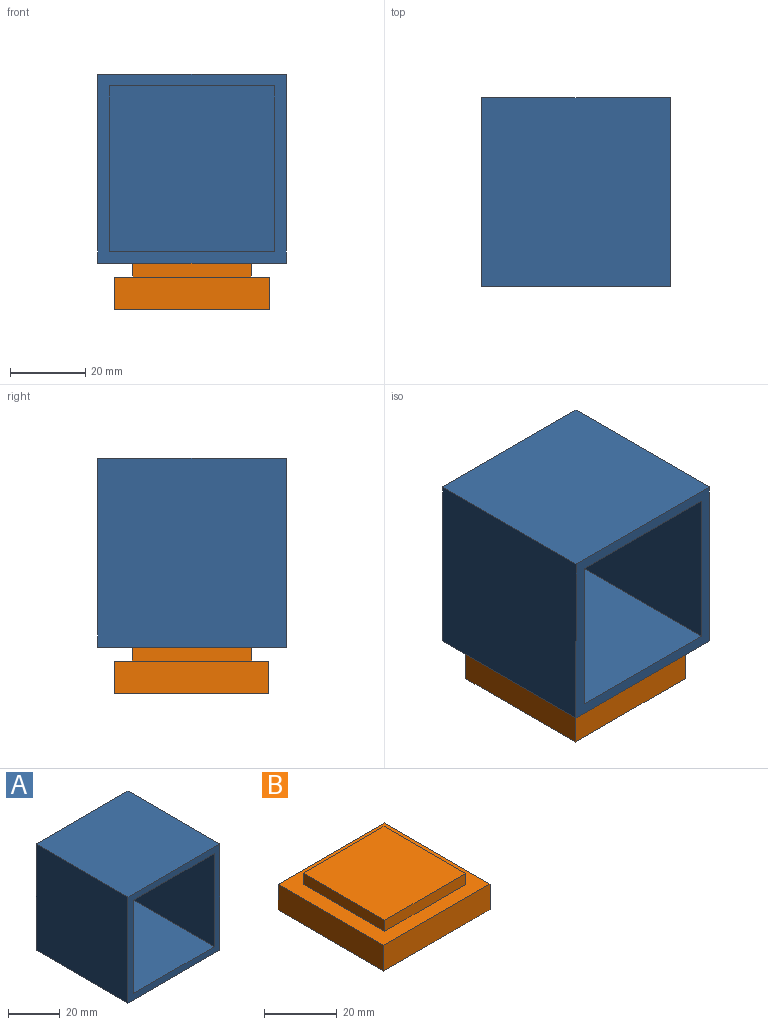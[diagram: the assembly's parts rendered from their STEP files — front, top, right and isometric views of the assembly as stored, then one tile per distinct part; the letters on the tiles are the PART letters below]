
ASSEMBLY  parts=2 mates=1
PART A: 11 faces, bbox 50.1x50.1x50.1 mm
  f0: plane 50.11x50.11mm, normal (0,-1,0), area 573.8mm2, adj f1,f2,f3,f4,f6,f7,f8,f9
  f1: plane 50.11x50.11mm, normal (0,0,1), area 2511.4mm2, adj f0,f2,f4,f5
  f2: plane 50.11x50.11mm, normal (-1,0,0), area 2511.4mm2, adj f0,f1,f3,f5
  f3: plane 50.11x50.11mm, normal (0,0,-1), area 2511.4mm2, adj f0,f2,f4,f5
  f4: plane 50.11x50.11mm, normal (1,0,0), area 2511.4mm2, adj f0,f1,f3,f5
  f5: plane 50.11x50.11mm, normal (0,1,0), area 2511.4mm2, adj f1,f2,f3,f4
  f6: plane 47.07x44.02mm, normal (0,0,-1), area 2071.8mm2, adj f0,f7,f9,f10
  f7: plane 47.07x44.02mm, normal (1,0,0), area 2071.8mm2, adj f0,f6,f8,f10
  f8: plane 47.07x44.02mm, normal (0,0,1), area 2071.8mm2, adj f0,f7,f9,f10
  f9: plane 47.07x44.02mm, normal (-1,0,0), area 2071.8mm2, adj f0,f6,f8,f10
  f10: plane 44.02x44.02mm, normal (0,-1,0), area 1937.6mm2, adj f6,f7,f8,f9
PART B: 11 faces, bbox 41.3x41.1x12.4 mm
  f0: plane 31.5x3.72mm, normal (0,-1,0), area 117.1mm2, adj f2,f3,f4,f5
  f1: plane 31.5x3.72mm, normal (0,1,0), area 117.1mm2, adj f2,f3,f4,f5
  f2: plane 31.75x31.5mm, normal (0,0,1), area 1000mm2, adj f0,f1,f3,f4
  f3: plane 31.75x3.72mm, normal (1,0,0), area 118mm2, adj f0,f1,f2,f5
  f4: plane 31.75x3.72mm, normal (-1,0,0), area 118mm2, adj f0,f1,f2,f5
  f5: plane 41.33x41.15mm, normal (0,0,1), area 700.5mm2, adj f0,f1,f3,f4,f6,f8,f9,f10
  f6: plane 41.33x8.64mm, normal (0,-1,0), area 356.9mm2, adj f5,f7,f9,f10
  f7: plane 41.33x41.15mm, normal (0,0,-1), area 1700.5mm2, adj f6,f8,f9,f10
  f8: plane 41.33x8.64mm, normal (0,1,0), area 356.9mm2, adj f5,f7,f9,f10
  f9: plane 41.15x8.64mm, normal (1,0,0), area 355.4mm2, adj f5,f6,f7,f8
  f10: plane 41.15x8.64mm, normal (-1,0,0), area 355.4mm2, adj f5,f6,f7,f8
PLACE A t=(30.94,40.89,-15.02)mm
PLACE B t=(30.74,40.93,-14.93)mm
MATE fastened A.f3 <-> B.f2  axis (0,0,-1) through (30.74,15.83,-34.51)mm
